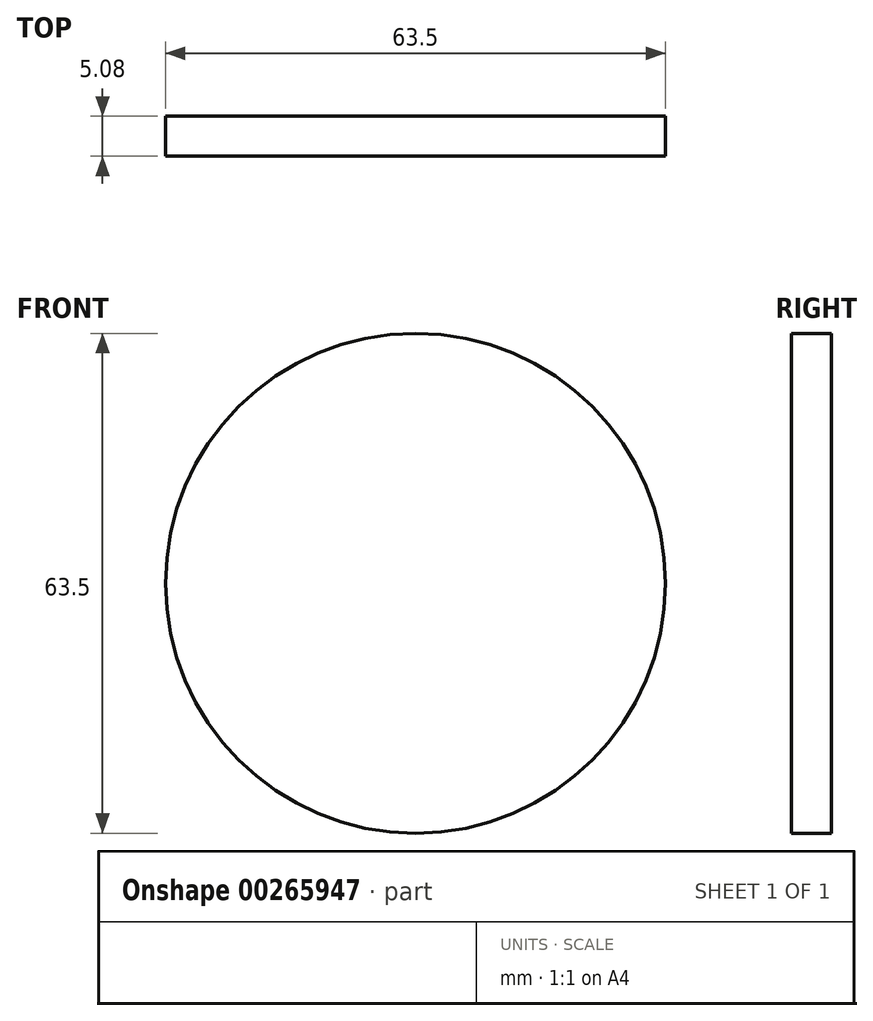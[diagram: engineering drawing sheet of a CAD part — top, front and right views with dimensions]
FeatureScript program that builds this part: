
annotation { "Feature Type Name" : "Feature", "Feature Type Description" : "" }
export const myFeature = defineFeature(function(context is Context, id is Id, definition is map)
    precondition{}
    {
        {
            var Q0;
            Q0=qCreatedBy(makeId("Front.planeOp"),FACE);
            var sketch = newSketch(context, id + "F0", { "sketchPlane" : qUnion([Q0])});
            skCircle(sketch, "E0", {"center": v(0, 0) * mm, "radius": 31.75 * mm});
            skSolve(sketch);
        }
        {
            var Q0;
            Q0 = qSketchRegion(id + "F0", true);
            extrude(context, id + "F1", {"entities" : qUnion([Q0]), "depth" : 5.08 * mm});
        }
    });
